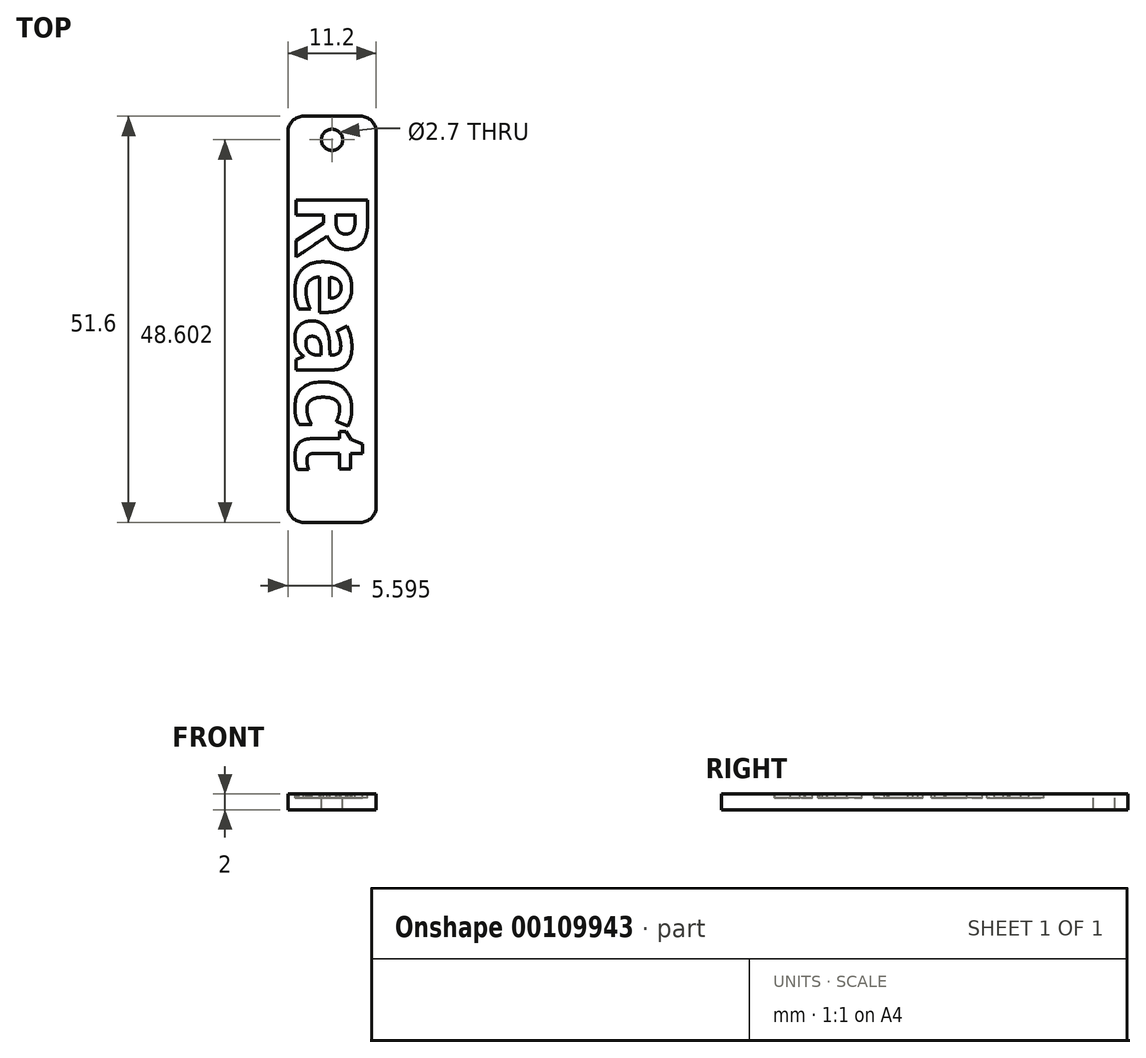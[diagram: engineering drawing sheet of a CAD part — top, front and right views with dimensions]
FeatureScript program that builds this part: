
annotation { "Feature Type Name" : "Feature", "Feature Type Description" : "" }
export const myFeature = defineFeature(function(context is Context, id is Id, definition is map)
    precondition{}
    {
        {
            var Q0;
            Q0=qCreatedBy(makeId("Top.planeOp"),FACE);
            var sketch = newSketch(context, id + "F0", { "sketchPlane" : qUnion([Q0])});
            skLineSegment(sketch, "E0.bottom", {"start": v(-49.26, 74.62) * mm, "end": v(-38.06, 74.62) * mm});
            skLineSegment(sketch, "E0.top", {"start": v(-49.26, 23.02) * mm, "end": v(-38.06, 23.02) * mm});
            skLineSegment(sketch, "E0.left", {"start": v(-49.26, 74.62) * mm, "end": v(-49.26, 23.02) * mm});
            skLineSegment(sketch, "E0.right", {"start": v(-38.06, 74.62) * mm, "end": v(-38.06, 23.02) * mm});
            skCircle(sketch, "E1", {"center": v(-43.66, 71.62) * mm, "radius": 1.35 * mm});
            skText(sketch, "E2", { "text": "React", "fontName": "OpenSans-Bold.ttf"});
            const initialGuessF0  = {"E2": [-0.04826, 0.06514, 0, -1, 0.0092]};
            skSetInitialGuess(sketch, initialGuessF0);
            skSolve(sketch);
        }
        {
            var Q0;
            Q0=makeQuery(id+"F0.imprint","IMPRINT",FACE,{"disambiguationData":[TD([[makeQuery(id+"F0.imprint","IMPRINT",EDGE,{"derivedFrom":sQuery(id+"F0.wireOp",EDGE,"E2.sketch_text.stroke-8")}),1.0]])]});
            var Q1;
            Q1=makeQuery(id+"F0.imprint","IMPRINT",FACE,{"disambiguationData":[TD([[makeQuery(id+"F0.imprint","IMPRINT",EDGE,{"derivedFrom":sQuery(id+"F0.wireOp",EDGE,"E2.sketch_text.stroke-14")}),-1.0]])]});
            var Q2;
            Q2=makeQuery(id+"F0.imprint","IMPRINT",FACE,{"disambiguationData":[TD([[makeQuery(id+"F0.imprint","IMPRINT",EDGE,{"derivedFrom":sQuery(id+"F0.wireOp",EDGE,"E2.sketch_text.stroke-32")}),-1.0]])]});
            var Q3;
            Q3=makeQuery(id+"F0.imprint","IMPRINT",FACE,{"disambiguationData":[TD([[makeQuery(id+"F0.imprint","IMPRINT",EDGE,{"derivedFrom":sQuery(id+"F0.wireOp",EDGE,"E2.sketch_text.stroke-49")}),-1.0]])]});
            var Q4;
            Q4=makeQuery(id+"F0.imprint","IMPRINT",FACE,{"disambiguationData":[TD([[makeQuery(id+"F0.imprint","IMPRINT",EDGE,{"derivedFrom":sQuery(id+"F0.wireOp",EDGE,"E2.sketch_text.stroke-69")}),-1.0]])]});
            var Q5;
            Q5=makeQuery(id+"F0.imprint","IMPRINT",FACE,{"disambiguationData":[TD([[makeQuery(id+"F0.imprint","IMPRINT",EDGE,{"derivedFrom":sQuery(id+"F0.wireOp",EDGE,"E0.bottom")}),-1.0]])]});
            var Q6;
            Q6=makeQuery(id+"F0.imprint","IMPRINT",FACE,{"disambiguationData":[TD([[makeQuery(id+"F0.imprint","IMPRINT",EDGE,{"derivedFrom":sQuery(id+"F0.wireOp",EDGE,"E2.sketch_text.stroke-0")}),-1.0]])]});
            var Q7;
            Q7=makeQuery(id+"F0.imprint","IMPRINT",FACE,{"disambiguationData":[TD([[makeQuery(id+"F0.imprint","IMPRINT",EDGE,{"derivedFrom":sQuery(id+"F0.wireOp",EDGE,"E2.sketch_text.stroke-49")}),1.0]])]});
            var Q8;
            Q8=makeQuery(id+"F0.imprint","IMPRINT",FACE,{"disambiguationData":[TD([[makeQuery(id+"F0.imprint","IMPRINT",EDGE,{"derivedFrom":sQuery(id+"F0.wireOp",EDGE,"E2.sketch_text.stroke-10")}),-1.0]])]});
            var Q9;
            Q9=makeQuery(id+"F0.imprint","IMPRINT",FACE,{"disambiguationData":[TD([[makeQuery(id+"F0.imprint","IMPRINT",EDGE,{"derivedFrom":sQuery(id+"F0.wireOp",EDGE,"E2.sketch_text.stroke-14")}),1.0]])]});
            var Q10;
            Q10=makeQuery(id+"F0.imprint","IMPRINT",FACE,{"disambiguationData":[TD([[makeQuery(id+"F0.imprint","IMPRINT",EDGE,{"derivedFrom":sQuery(id+"F0.wireOp",EDGE,"E2.sketch_text.stroke-34")}),-1.0]])]});
            var Q11;
            Q11=makeQuery(id+"F0.imprint","IMPRINT",FACE,{"disambiguationData":[TD([[makeQuery(id+"F0.imprint","IMPRINT",EDGE,{"derivedFrom":sQuery(id+"F0.wireOp",EDGE,"E2.sketch_text.stroke-0")}),1.0]])]});
            var Q12;
            Q12=makeQuery(id+"F0.imprint","IMPRINT",FACE,{"disambiguationData":[TD([[makeQuery(id+"F0.imprint","IMPRINT",EDGE,{"derivedFrom":sQuery(id+"F0.wireOp",EDGE,"E2.sketch_text.stroke-19")}),1.0]])]});
            var Q13;
            Q13=makeQuery(id+"F0.imprint","IMPRINT",FACE,{"disambiguationData":[TD([[makeQuery(id+"F0.imprint","IMPRINT",EDGE,{"derivedFrom":sQuery(id+"F0.wireOp",EDGE,"E2.sketch_text.stroke-57")}),1.0]])]});
            var Q14;
            Q14=makeQuery(id+"F0.imprint","IMPRINT",FACE,{"disambiguationData":[TD([[makeQuery(id+"F0.imprint","IMPRINT",EDGE,{"derivedFrom":sQuery(id+"F0.wireOp",EDGE,"E2.sketch_text.stroke-78")}),-1.0]])]});
            extrude(context, id + "F1", {"entities" : qUnion([Q0, Q1, Q2, Q3, Q4, Q5, Q6, Q7, Q8, Q9, Q10, Q11, Q12, Q13, Q14]), "oppositeDirection" : true, "depth" : 2 * mm});
        }
        {
            var Q0;
            Q0=makeQuery(id+"F0.imprint","IMPRINT",FACE,{"disambiguationData":[TD([[makeQuery(id+"F0.imprint","IMPRINT",EDGE,{"derivedFrom":sQuery(id+"F0.wireOp",EDGE,"E2.sketch_text.stroke-0")}),-1.0]])]});
            var Q1;
            Q1=makeQuery(id+"F0.imprint","IMPRINT",FACE,{"disambiguationData":[TD([[makeQuery(id+"F0.imprint","IMPRINT",EDGE,{"derivedFrom":sQuery(id+"F0.wireOp",EDGE,"E2.sketch_text.stroke-16")}),-1.0]])]});
            var Q2;
            Q2=makeQuery(id+"F0.imprint","IMPRINT",FACE,{"disambiguationData":[TD([[makeQuery(id+"F0.imprint","IMPRINT",EDGE,{"derivedFrom":sQuery(id+"F0.wireOp",EDGE,"E2.sketch_text.stroke-28")}),-1.0]])]});
            var Q3;
            Q3=makeQuery(id+"F0.imprint","IMPRINT",FACE,{"disambiguationData":[TD([[makeQuery(id+"F0.imprint","IMPRINT",EDGE,{"derivedFrom":sQuery(id+"F0.wireOp",EDGE,"E2.sketch_text.stroke-36")}),-1.0]])]});
            var Q4;
            Q4=makeQuery(id+"F0.imprint","IMPRINT",FACE,{"disambiguationData":[TD([[makeQuery(id+"F0.imprint","IMPRINT",EDGE,{"derivedFrom":sQuery(id+"F0.wireOp",EDGE,"E2.sketch_text.stroke-49")}),-1.0]])]});
            var Q5;
            Q5=makeQuery(id+"F0.imprint","IMPRINT",FACE,{"disambiguationData":[TD([[makeQuery(id+"F0.imprint","IMPRINT",EDGE,{"derivedFrom":sQuery(id+"F0.wireOp",EDGE,"E2.sketch_text.stroke-69")}),-1.0]])]});
            var Q6;
            Q6=makeQuery(id+"F0.imprint","IMPRINT",FACE,{"disambiguationData":[TD([[makeQuery(id+"F0.imprint","IMPRINT",EDGE,{"derivedFrom":sQuery(id+"F0.wireOp",EDGE,"E2.sketch_text.stroke-10")}),-1.0]])]});
            var Q7;
            Q7=makeQuery(id+"F0.imprint","IMPRINT",FACE,{"disambiguationData":[TD([[makeQuery(id+"F0.imprint","IMPRINT",EDGE,{"derivedFrom":sQuery(id+"F0.wireOp",EDGE,"E2.sketch_text.stroke-78")}),-1.0]])]});
            var Q8;
            Q8=qConstructionFilter(qBodyType(qCreatedBy(id+"F0",EDGE),BodyType.WIRE),ConstructionObject.NO);
            extrude(context, id + "F2", {"entities" : qUnion([Q0, Q1, Q2, Q3, Q4, Q5, Q6, Q7]), "operationType" : NewBodyOperationType.REMOVE, "surfaceEntities" : qUnion([Q8]), "oppositeDirection" : true, "depth" : .5 * mm});
        }
        {
            var Q0;
            Q0=makeQuery(id+"F1.opExtrude","SWEPT_EDGE",EDGE,{"disambiguationData":[OSD([sQuery(id+"F0.wireOp",EDGE,"E0.bottom"),sQuery(id+"F0.wireOp",EDGE,"E0.left")])]});
            var Q1;
            Q1=makeQuery(id+"F1.opExtrude","SWEPT_EDGE",EDGE,{"disambiguationData":[OSD([sQuery(id+"F0.wireOp",EDGE,"E0.bottom"),sQuery(id+"F0.wireOp",EDGE,"E0.right")])]});
            var Q2;
            Q2=makeQuery(id+"F1.opExtrude","SWEPT_EDGE",EDGE,{"disambiguationData":[OSD([sQuery(id+"F0.wireOp",EDGE,"E0.top"),sQuery(id+"F0.wireOp",EDGE,"E0.right")])]});
            var Q3;
            Q3=makeQuery(id+"F1.opExtrude","SWEPT_EDGE",EDGE,{"disambiguationData":[OSD([sQuery(id+"F0.wireOp",EDGE,"E0.top"),sQuery(id+"F0.wireOp",EDGE,"E0.left")])]});
            fillet(context, id + "F3", {"entities" : qUnion([Q0, Q1, Q2, Q3]), "radius" : 2 * mm, "tangentPropagation" : true, "allowEdgeOverflow" : false});
        }
    });
